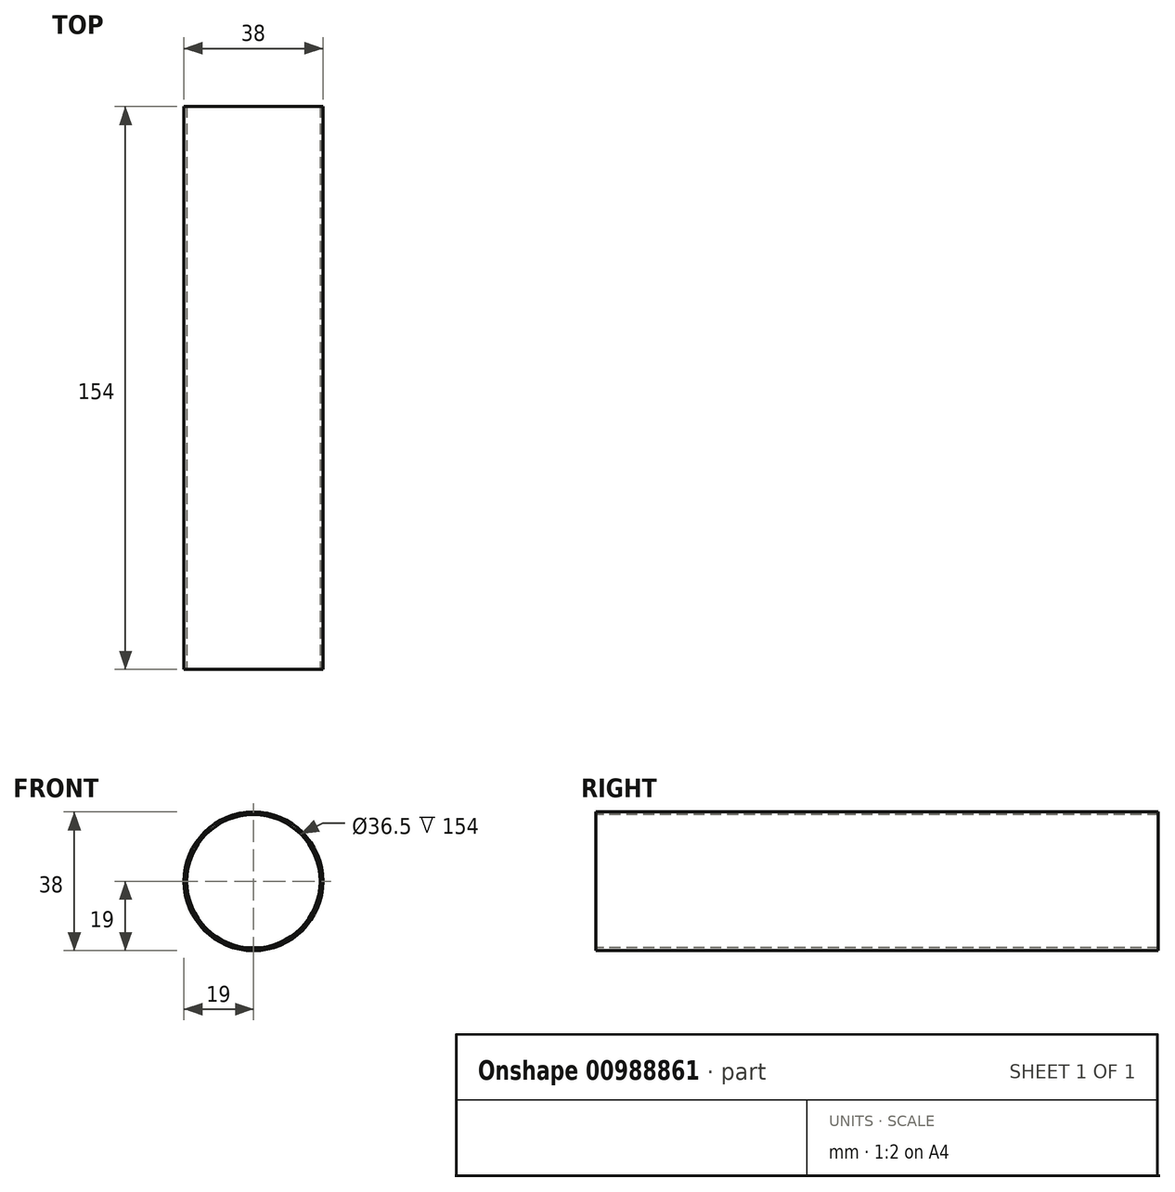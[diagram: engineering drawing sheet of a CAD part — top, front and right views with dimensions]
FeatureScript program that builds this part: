
annotation { "Feature Type Name" : "Feature", "Feature Type Description" : "" }
export const myFeature = defineFeature(function(context is Context, id is Id, definition is map)
    precondition{}
    {
        {
            var Q0;
            Q0=qCreatedBy(makeId("Front.planeOp"),FACE);
            var sketch = newSketch(context, id + "F0", { "sketchPlane" : qUnion([Q0])});
            skCircle(sketch, "E0", {"center": v(0, 0) * mm, "radius": 19 * mm});
            skCircle(sketch, "E1", {"center": v(0, 0) * mm, "radius": 18.25 * mm});
            skSolve(sketch);
        }
        {
            var Q0;
            Q0 = qSketchRegion(id + "F0", true);
            extrude(context, id + "F1", {"entities" : qUnion([Q0]), "oppositeDirection" : true, "depth" : 154 * mm, "offsetDistance" : 25 * mm});
        }
    });
